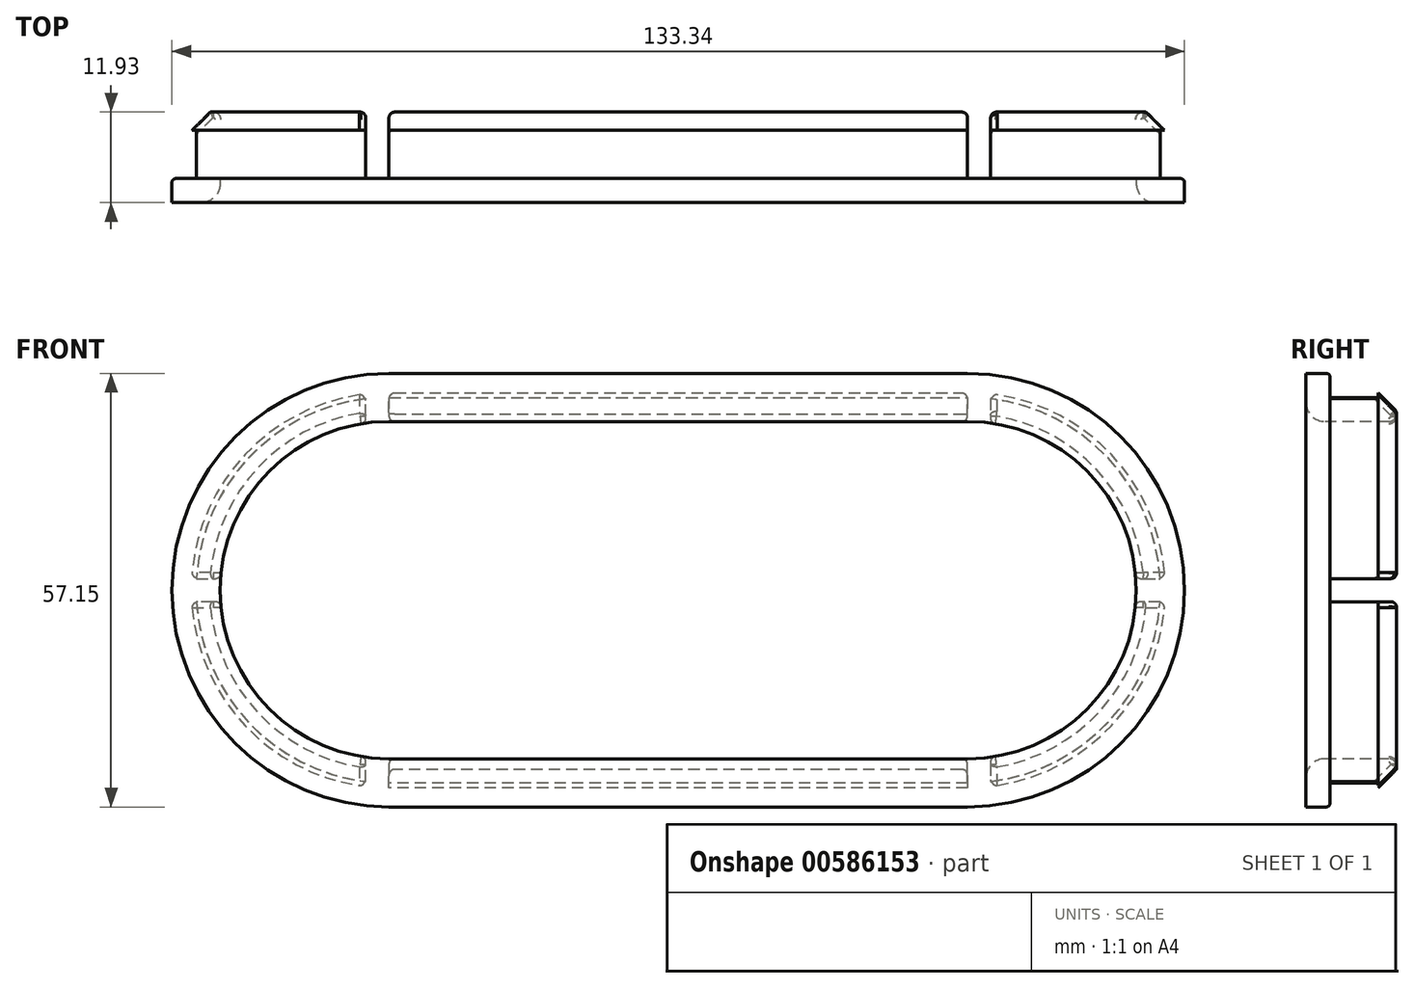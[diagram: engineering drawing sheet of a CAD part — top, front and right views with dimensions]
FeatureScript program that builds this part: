
annotation { "Feature Type Name" : "Feature", "Feature Type Description" : "" }
export const myFeature = defineFeature(function(context is Context, id is Id, definition is map)
    precondition{}
    {
        {
            var Q0;
            Q0=qCreatedBy(makeId("Front.planeOp"),FACE);
            var sketch = newSketch(context, id + "F0", { "sketchPlane" : qUnion([Q0])});
            skArc(sketch, "E0", {"start": v(-38.1, 28.58) * mm, "mid": v(-66.68, 0) * mm, "end": v(-38.1, -28.58) * mm});
            skArc(sketch, "E1", {"start": v(38.1, -28.58) * mm, "mid": v(66.68, 0) * mm, "end": v(38.1, 28.58) * mm});
            skLineSegment(sketch, "E2", {"start": v(-38.1, 28.58) * mm, "end": v(38.1, 28.58) * mm});
            skLineSegment(sketch, "E3", {"start": v(38.1, -28.58) * mm, "end": v(-38.1, -28.58) * mm});
            skArc(sketch, "E4", {"start": v(-38.1, 25.27) * mm, "mid": v(-63.37, 0) * mm, "end": v(-38.1, -25.27) * mm});
            skArc(sketch, "E5", {"start": v(38.1, -25.27) * mm, "mid": v(63.37, 0) * mm, "end": v(38.1, 25.27) * mm});
            skLineSegment(sketch, "E6", {"start": v(-38.1, 25.27) * mm, "end": v(38.1, 25.27) * mm});
            skLineSegment(sketch, "E7", {"start": v(38.1, -25.27) * mm, "end": v(-38.1, -25.27) * mm});
            skArc(sketch, "E8", {"start": v(-38.1, 22.23) * mm, "mid": v(-60.33, 0) * mm, "end": v(-38.1, -22.23) * mm});
            skArc(sketch, "E9", {"start": v(38.1, -22.23) * mm, "mid": v(60.33, 0) * mm, "end": v(38.1, 22.23) * mm});
            skLineSegment(sketch, "E10", {"start": v(-38.1, 22.23) * mm, "end": v(38.1, 22.23) * mm});
            skLineSegment(sketch, "E11", {"start": v(-38.1, -22.23) * mm, "end": v(38.1, -22.23) * mm});
            skSolve(sketch);
        }
        {
            var Q0;
            Q0 = qSketchRegion(id + "F0", true);
            extrude(context, id + "F1", {"entities" : qUnion([Q0]), "depth" : 3.17 * mm, "offsetDistance" : 25.4 * mm});
        }
        {
            var Q0;
            Q0=makeQuery(id+"F1.opExtrude","CAP_FACE",FACE,{"disambiguationData":[OSD([sQuery(id+"F0.wireOp",EDGE,"E0"),sQuery(id+"F0.wireOp",EDGE,"E1"),sQuery(id+"F0.wireOp",EDGE,"E2"),sQuery(id+"F0.wireOp",EDGE,"E3"),sQuery(id+"F0.wireOp",EDGE,"E4"),sQuery(id+"F0.wireOp",EDGE,"E5"),sQuery(id+"F0.wireOp",EDGE,"E6"),sQuery(id+"F0.wireOp",EDGE,"E7")])],"isStart":false});
            var sketch = newSketch(context, id + "F2", { "sketchPlane" : qUnion([Q0])});
            skArc(sketch, "E12", {"start": v(-38.1, 22.23) * mm, "mid": v(-60.33, 0) * mm, "end": v(-38.1, -22.23) * mm});
            skArc(sketch, "E13", {"start": v(38.1, -22.23) * mm, "mid": v(60.33, 0) * mm, "end": v(38.1, 22.23) * mm});
            skLineSegment(sketch, "E14", {"start": v(-38.1, 22.22) * mm, "end": v(38.1, 22.23) * mm});
            skLineSegment(sketch, "E15", {"start": v(38.1, -22.23) * mm, "end": v(-38.1, -22.23) * mm});
            skArc(sketch, "E16", {"start": v(-38.1, 25.4) * mm, "mid": v(-63.5, 0) * mm, "end": v(-38.1, -25.4) * mm});
            skArc(sketch, "E17", {"start": v(38.1, -25.4) * mm, "mid": v(63.5, 0) * mm, "end": v(38.1, 25.4) * mm});
            skLineSegment(sketch, "E18", {"start": v(-38.1, 25.4) * mm, "end": v(38.1, 25.4) * mm});
            skLineSegment(sketch, "E19", {"start": v(38.1, -25.4) * mm, "end": v(-38.1, -25.4) * mm});
            skSolve(sketch);
        }
        {
            var Q0;
            Q0 = qSketchRegion(id + "F2", true);
            extrude(context, id + "F3", {"entities" : qUnion([Q0]), "operationType" : NewBodyOperationType.ADD, "oppositeDirection" : true, "depth" : 11.94 * mm, "offsetDistance" : 25.4 * mm});
        }
        {
            var Q0;
            Q0=makeQuery(id+"F3.opExtrude","CAP_FACE",FACE,{"disambiguationData":[OSD([sQuery(id+"F2.wireOp",EDGE,"E12"),sQuery(id+"F2.wireOp",EDGE,"E13"),sQuery(id+"F2.wireOp",EDGE,"E14"),sQuery(id+"F2.wireOp",EDGE,"E15"),sQuery(id+"F2.wireOp",EDGE,"E16"),sQuery(id+"F2.wireOp",EDGE,"E17"),sQuery(id+"F2.wireOp",EDGE,"E18"),sQuery(id+"F2.wireOp",EDGE,"E19")])],"isStart":false});
            var sketch = newSketch(context, id + "F4", { "sketchPlane" : qUnion([Q0])});
            skArc(sketch, "E20", {"start": v(-38.1, 26.16) * mm, "mid": v(-64.26, 0) * mm, "end": v(-38.1, -26.16) * mm});
            skArc(sketch, "E21", {"start": v(38.1, -26.16) * mm, "mid": v(64.26, 0) * mm, "end": v(38.1, 26.16) * mm});
            skLineSegment(sketch, "E22", {"start": v(-38.1, 26.16) * mm, "end": v(38.1, 26.16) * mm});
            skLineSegment(sketch, "E23", {"start": v(38.1, -26.16) * mm, "end": v(-38.1, -26.16) * mm});
            skArc(sketch, "E24", {"start": v(-38.1, 25.4) * mm, "mid": v(-63.5, 0) * mm, "end": v(-38.1, -25.4) * mm});
            skArc(sketch, "E25", {"start": v(38.1, -25.4) * mm, "mid": v(63.5, 0) * mm, "end": v(38.1, 25.4) * mm});
            skLineSegment(sketch, "E26", {"start": v(-38.1, 25.4) * mm, "end": v(38.1, 25.4) * mm});
            skLineSegment(sketch, "E27", {"start": v(136.2, 25.4) * mm, "end": v(136.2, -25.4) * mm});
            skLineSegment(sketch, "E28", {"start": v(38.1, -25.4) * mm, "end": v(-38.1, -25.4) * mm});
            skSolve(sketch);
        }
        {
            var Q0;
            Q0 = qSketchRegion(id + "F4", true);
            extrude(context, id + "F5", {"entities" : qUnion([Q0]), "operationType" : NewBodyOperationType.ADD, "oppositeDirection" : true, "depth" : 2.41 * mm, "offsetDistance" : 25.4 * mm});
        }
        {
            var Q0;
            Q0=makeQuery(id+"F5.opExtrude","CAP_EDGE",EDGE,{"disambiguationData":[OSD([sQuery(id+"F4.wireOp",EDGE,"E22")])],"isStart":true});
            chamfer(context, id + "F6", {"entities" : qUnion([Q0]), "width" : 2.54 * mm, "tangentPropagation" : true});
        }
        {
            var Q0;
            Q0=makeQuery(id+"F3.opExtrude","CAP_EDGE",EDGE,{"disambiguationData":[OSD([sQuery(id+"F2.wireOp",EDGE,"E14")])],"isStart":true});
            fillet(context, id + "F7", {"entities" : qUnion([Q0]), "radius" : 2.54 * mm, "tangentPropagation" : true, "allowEdgeOverflow" : false});
        }
        {
            var Q0;
            Q0=qCreatedBy(makeId("Front.planeOp"),FACE);
            var sketch = newSketch(context, id + "F8", { "sketchPlane" : qUnion([Q0])});
            skLineSegment(sketch, "E29", {"start": v(101.6, -1.52) * mm, "end": v(-101.6, -1.52) * mm});
            skLineSegment(sketch, "E30", {"start": v(-101.6, -1.52) * mm, "end": v(-101.6, 1.52) * mm});
            skLineSegment(sketch, "E31", {"start": v(-101.6, 1.52) * mm, "end": v(101.6, 1.52) * mm});
            skLineSegment(sketch, "E32", {"start": v(101.6, 1.52) * mm, "end": v(101.6, -1.52) * mm});
            skSolve(sketch);
        }
        {
            var Q0;
            Q0 = qSketchRegion(id + "F8", true);
            extrude(context, id + "F9", {"entities" : qUnion([Q0]), "operationType" : NewBodyOperationType.REMOVE, "oppositeDirection" : true, "depth" : 25.4 * mm, "offsetDistance" : 25.4 * mm});
        }
        {
            var Q0;
            Q0=qCreatedBy(makeId("Front.planeOp"),FACE);
            var sketch = newSketch(context, id + "F10", { "sketchPlane" : qUnion([Q0])});
            skLineSegment(sketch, "E33", {"start": v(41.15, 38.1) * mm, "end": v(41.15, -38.1) * mm});
            skLineSegment(sketch, "E34", {"start": v(41.15, -38.1) * mm, "end": v(38.1, -38.1) * mm});
            skLineSegment(sketch, "E35", {"start": v(38.1, -38.1) * mm, "end": v(38.1, 38.1) * mm});
            skLineSegment(sketch, "E36", {"start": v(38.1, 38.1) * mm, "end": v(41.15, 38.1) * mm});
            skLineSegment(sketch, "E37", {"start": v(-38.1, 38.1) * mm, "end": v(-38.1, -38.1) * mm});
            skLineSegment(sketch, "E38", {"start": v(-38.1, -38.1) * mm, "end": v(-41.15, -38.1) * mm});
            skLineSegment(sketch, "E39", {"start": v(-41.15, -38.1) * mm, "end": v(-41.15, 38.1) * mm});
            skLineSegment(sketch, "E40", {"start": v(-41.15, 38.1) * mm, "end": v(-38.1, 38.1) * mm});
            skSolve(sketch);
        }
        {
            var Q0;
            Q0 = qSketchRegion(id + "F10", true);
            extrude(context, id + "F11", {"entities" : qUnion([Q0]), "operationType" : NewBodyOperationType.REMOVE, "oppositeDirection" : true, "depth" : 25.4 * mm, "offsetDistance" : 25.4 * mm});
        }
        {
            var Q0;
            Q0=makeQuery(id+"F3.opExtrude","CAP_EDGE",EDGE,{"disambiguationData":[OSD([sQuery(id+"F2.wireOp",EDGE,"E14")])],"isStart":false});
            var Q1;
            {var subQ0=sQuery(id+"F2.wireOp",EDGE,"E14");var subQ1=sQuery(id+"F2.wireOp",EDGE,"E13");Q1=makeQuery(id+"F9.boolean.opBoolean","SPLIT",EDGE,{"disambiguationData":[TD([makeQuery(id+"F3.opExtrude","SWEPT_FACE",FACE,{"disambiguationData":[OSD([subQ0])]})])],"derivedFrom":makeQuery(id+"F3.opExtrude","CAP_EDGE",EDGE,{"disambiguationData":[OSD([subQ1])],"isStart":false})});}
            var Q2;
            {var subQ0=sQuery(id+"F2.wireOp",EDGE,"E15");var subQ1=sQuery(id+"F2.wireOp",EDGE,"E13");Q2=makeQuery(id+"F9.boolean.opBoolean","SPLIT",EDGE,{"disambiguationData":[TD([makeQuery(id+"F3.opExtrude","SWEPT_FACE",FACE,{"disambiguationData":[OSD([subQ0])]})])],"derivedFrom":makeQuery(id+"F3.opExtrude","CAP_EDGE",EDGE,{"disambiguationData":[OSD([subQ1])],"isStart":false})});}
            var Q3;
            Q3=makeQuery(id+"F3.opExtrude","CAP_EDGE",EDGE,{"disambiguationData":[OSD([sQuery(id+"F2.wireOp",EDGE,"E15")])],"isStart":false});
            var Q4;
            {var subQ0=sQuery(id+"F2.wireOp",EDGE,"E15");var subQ1=sQuery(id+"F2.wireOp",EDGE,"E12");Q4=makeQuery(id+"F9.boolean.opBoolean","SPLIT",EDGE,{"disambiguationData":[TD([makeQuery(id+"F3.opExtrude","SWEPT_FACE",FACE,{"disambiguationData":[OSD([subQ0])]})])],"derivedFrom":makeQuery(id+"F3.opExtrude","CAP_EDGE",EDGE,{"disambiguationData":[OSD([subQ1])],"isStart":false})});}
            var Q5;
            {var subQ0=sQuery(id+"F2.wireOp",EDGE,"E14");var subQ1=sQuery(id+"F2.wireOp",EDGE,"E12");Q5=makeQuery(id+"F9.boolean.opBoolean","SPLIT",EDGE,{"disambiguationData":[TD([makeQuery(id+"F3.opExtrude","SWEPT_FACE",FACE,{"disambiguationData":[OSD([subQ0])]})])],"derivedFrom":makeQuery(id+"F3.opExtrude","CAP_EDGE",EDGE,{"disambiguationData":[OSD([subQ1])],"isStart":false})});}
            fillet(context, id + "F12", {"entities" : qUnion([Q0, Q1, Q2, Q3, Q4, Q5]), "radius" : 1.02 * mm, "tangentPropagation" : true, "allowEdgeOverflow" : false});
        }
        {
            var Q0;
            {var subQ0=sQuery(id+"F4.wireOp",EDGE,"E22");Q0=makeQuery(id+"F6.opChamfer","BLEND_EDGE",EDGE,{"blendedFrom":[makeQuery(id+"F5.opExtrude","CAP_EDGE",EDGE,{"disambiguationData":[OSD([subQ0])],"isStart":true}),makeQuery(id+"F5.boolean.opBoolean","MERGE",FACE,{"derivedFrom":[makeQuery(id+"F3.opExtrude","CAP_FACE",FACE,{"disambiguationData":[OSD([sQuery(id+"F2.wireOp",EDGE,"E12"),sQuery(id+"F2.wireOp",EDGE,"E13"),sQuery(id+"F2.wireOp",EDGE,"E14"),sQuery(id+"F2.wireOp",EDGE,"E15"),sQuery(id+"F2.wireOp",EDGE,"E16"),sQuery(id+"F2.wireOp",EDGE,"E17"),sQuery(id+"F2.wireOp",EDGE,"E18"),sQuery(id+"F2.wireOp",EDGE,"E19")])],"isStart":false}),makeQuery(id+"F5.opExtrude","CAP_FACE",FACE,{"disambiguationData":[OSD([sQuery(id+"F4.wireOp",EDGE,"E20"),sQuery(id+"F4.wireOp",EDGE,"E21"),subQ0,sQuery(id+"F4.wireOp",EDGE,"E23"),sQuery(id+"F4.wireOp",EDGE,"E24"),sQuery(id+"F4.wireOp",EDGE,"E25"),sQuery(id+"F4.wireOp",EDGE,"E26"),sQuery(id+"F4.wireOp",EDGE,"E28")])],"isStart":true})]})],"blendedInto":[makeQuery(id+"F5.boolean.opBoolean","MERGE",FACE,{"derivedFrom":[makeQuery(id+"F3.opExtrude","CAP_FACE",FACE,{"disambiguationData":[OSD([sQuery(id+"F2.wireOp",EDGE,"E12"),sQuery(id+"F2.wireOp",EDGE,"E13"),sQuery(id+"F2.wireOp",EDGE,"E14"),sQuery(id+"F2.wireOp",EDGE,"E15"),sQuery(id+"F2.wireOp",EDGE,"E16"),sQuery(id+"F2.wireOp",EDGE,"E17"),sQuery(id+"F2.wireOp",EDGE,"E18"),sQuery(id+"F2.wireOp",EDGE,"E19")])],"isStart":false}),makeQuery(id+"F5.opExtrude","CAP_FACE",FACE,{"disambiguationData":[OSD([sQuery(id+"F4.wireOp",EDGE,"E20"),sQuery(id+"F4.wireOp",EDGE,"E21"),subQ0,sQuery(id+"F4.wireOp",EDGE,"E23"),sQuery(id+"F4.wireOp",EDGE,"E24"),sQuery(id+"F4.wireOp",EDGE,"E25"),sQuery(id+"F4.wireOp",EDGE,"E26"),sQuery(id+"F4.wireOp",EDGE,"E28")])],"isStart":true})]})]});}
            var Q1;
            {var subQ0=sQuery(id+"F4.wireOp",EDGE,"E22");var subQ1=sQuery(id+"F4.wireOp",EDGE,"E20");var subQ2=makeQuery(id+"F3.opExtrude","CAP_FACE",FACE,{"disambiguationData":[OSD([sQuery(id+"F2.wireOp",EDGE,"E12"),sQuery(id+"F2.wireOp",EDGE,"E13"),sQuery(id+"F2.wireOp",EDGE,"E14"),sQuery(id+"F2.wireOp",EDGE,"E15"),sQuery(id+"F2.wireOp",EDGE,"E16"),sQuery(id+"F2.wireOp",EDGE,"E17"),sQuery(id+"F2.wireOp",EDGE,"E18"),sQuery(id+"F2.wireOp",EDGE,"E19")])],"isStart":false});var subQ3=makeQuery(id+"F5.opExtrude","CAP_FACE",FACE,{"disambiguationData":[OSD([subQ1,sQuery(id+"F4.wireOp",EDGE,"E21"),subQ0,sQuery(id+"F4.wireOp",EDGE,"E23"),sQuery(id+"F4.wireOp",EDGE,"E24"),sQuery(id+"F4.wireOp",EDGE,"E25"),sQuery(id+"F4.wireOp",EDGE,"E26"),sQuery(id+"F4.wireOp",EDGE,"E28")])],"isStart":true});Q1=makeQuery(id+"F9.boolean.opBoolean","SPLIT",EDGE,{"disambiguationData":[TD([makeQuery(id+"F6.opChamfer","BLEND_FACE",FACE,{"disambiguationData":[OSD([subQ0])]})])],"derivedFrom":makeQuery(id+"F6.opChamfer","BLEND_EDGE",EDGE,{"blendedFrom":[makeQuery(id+"F5.opExtrude","CAP_EDGE",EDGE,{"disambiguationData":[OSD([subQ1])],"isStart":true}),makeQuery(id+"F5.boolean.opBoolean","MERGE",FACE,{"derivedFrom":[subQ2,subQ3]})],"blendedInto":[makeQuery(id+"F5.boolean.opBoolean","MERGE",FACE,{"derivedFrom":[subQ2,subQ3]})]})});}
            var Q2;
            {var subQ0=sQuery(id+"F2.wireOp",EDGE,"E13");var subQ1=makeQuery(id+"F3.opExtrude","SWEPT_FACE",FACE,{"disambiguationData":[OSD([subQ0])]});var subQ2=sQuery(id+"F4.wireOp",EDGE,"E20");var subQ4=sQuery(id+"F2.wireOp",EDGE,"E17");var subQ5=sQuery(id+"F4.wireOp",EDGE,"E28");var subQ6=sQuery(id+"F4.wireOp",EDGE,"E26");var subQ7=sQuery(id+"F4.wireOp",EDGE,"E25");var subQ8=sQuery(id+"F4.wireOp",EDGE,"E24");var subQ9=sQuery(id+"F4.wireOp",EDGE,"E23");var subQ10=sQuery(id+"F4.wireOp",EDGE,"E22");var subQ11=sQuery(id+"F4.wireOp",EDGE,"E21");var subQ12=sQuery(id+"F2.wireOp",EDGE,"E15");var subQ13=sQuery(id+"F2.wireOp",EDGE,"E12");var subQ14=makeQuery(id+"F3.opExtrude","CAP_FACE",FACE,{"disambiguationData":[OSD([subQ13,subQ0,sQuery(id+"F2.wireOp",EDGE,"E14"),subQ12,sQuery(id+"F2.wireOp",EDGE,"E16"),subQ4,sQuery(id+"F2.wireOp",EDGE,"E18"),sQuery(id+"F2.wireOp",EDGE,"E19")])],"isStart":false});var subQ15=makeQuery(id+"F5.opExtrude","CAP_FACE",FACE,{"disambiguationData":[OSD([subQ2,subQ11,subQ10,subQ9,subQ8,subQ7,subQ6,subQ5])],"isStart":true});var subQ18=makeQuery(id+"F3.opExtrude","SWEPT_FACE",FACE,{"disambiguationData":[OSD([subQ12])]});Q2=makeQuery(id+"F12.opFillet","BLEND_EDGE",EDGE,{"blendedFrom":[makeQuery(id+"F9.boolean.opBoolean","SPLIT",EDGE,{"disambiguationData":[TD([subQ18])],"derivedFrom":makeQuery(id+"F3.opExtrude","CAP_EDGE",EDGE,{"disambiguationData":[OSD([subQ0])],"isStart":false})}),makeQuery(id+"F11.boolean.opBoolean","SPLIT",FACE,{"disambiguationData":[TD([subQ1])],"derivedFrom":makeQuery(id+"F9.boolean.opBoolean","SPLIT",FACE,{"disambiguationData":[TD([subQ18])],"derivedFrom":makeQuery(id+"F5.boolean.opBoolean","MERGE",FACE,{"derivedFrom":[subQ14,subQ15]})})})],"blendedInto":[makeQuery(id+"F11.boolean.opBoolean","SPLIT",FACE,{"disambiguationData":[TD([subQ1])],"derivedFrom":makeQuery(id+"F9.boolean.opBoolean","SPLIT",FACE,{"disambiguationData":[TD([subQ18])],"derivedFrom":makeQuery(id+"F5.boolean.opBoolean","MERGE",FACE,{"derivedFrom":[subQ14,subQ15]})})})]});}
            var Q3;
            {var subQ0=sQuery(id+"F2.wireOp",EDGE,"E15");var subQ1=makeQuery(id+"F3.opExtrude","SWEPT_FACE",FACE,{"disambiguationData":[OSD([subQ0])]});var subQ2=sQuery(id+"F4.wireOp",EDGE,"E23");var subQ4=sQuery(id+"F4.wireOp",EDGE,"E20");var subQ5=sQuery(id+"F2.wireOp",EDGE,"E13");var subQ6=sQuery(id+"F4.wireOp",EDGE,"E21");var subQ7=sQuery(id+"F2.wireOp",EDGE,"E12");Q3=makeQuery(id+"F12.opFillet","BLEND_EDGE",EDGE,{"blendedFrom":[makeQuery(id+"F3.opExtrude","CAP_EDGE",EDGE,{"disambiguationData":[OSD([subQ0])],"isStart":false}),makeQuery(id+"F11.boolean.opBoolean","SPLIT",FACE,{"disambiguationData":[TD([subQ1])],"derivedFrom":makeQuery(id+"F9.boolean.opBoolean","SPLIT",FACE,{"disambiguationData":[TD([subQ1])],"derivedFrom":makeQuery(id+"F5.boolean.opBoolean","MERGE",FACE,{"derivedFrom":[makeQuery(id+"F3.opExtrude","CAP_FACE",FACE,{"disambiguationData":[OSD([subQ7,subQ5,sQuery(id+"F2.wireOp",EDGE,"E14"),subQ0,sQuery(id+"F2.wireOp",EDGE,"E16"),sQuery(id+"F2.wireOp",EDGE,"E17"),sQuery(id+"F2.wireOp",EDGE,"E18"),sQuery(id+"F2.wireOp",EDGE,"E19")])],"isStart":false}),makeQuery(id+"F5.opExtrude","CAP_FACE",FACE,{"disambiguationData":[OSD([subQ4,subQ6,sQuery(id+"F4.wireOp",EDGE,"E22"),subQ2,sQuery(id+"F4.wireOp",EDGE,"E24"),sQuery(id+"F4.wireOp",EDGE,"E25"),sQuery(id+"F4.wireOp",EDGE,"E26"),sQuery(id+"F4.wireOp",EDGE,"E28")])],"isStart":true})]})})})],"blendedInto":[makeQuery(id+"F11.boolean.opBoolean","SPLIT",FACE,{"disambiguationData":[TD([subQ1])],"derivedFrom":makeQuery(id+"F9.boolean.opBoolean","SPLIT",FACE,{"disambiguationData":[TD([subQ1])],"derivedFrom":makeQuery(id+"F5.boolean.opBoolean","MERGE",FACE,{"derivedFrom":[makeQuery(id+"F3.opExtrude","CAP_FACE",FACE,{"disambiguationData":[OSD([subQ7,subQ5,sQuery(id+"F2.wireOp",EDGE,"E14"),subQ0,sQuery(id+"F2.wireOp",EDGE,"E16"),sQuery(id+"F2.wireOp",EDGE,"E17"),sQuery(id+"F2.wireOp",EDGE,"E18"),sQuery(id+"F2.wireOp",EDGE,"E19")])],"isStart":false}),makeQuery(id+"F5.opExtrude","CAP_FACE",FACE,{"disambiguationData":[OSD([subQ4,subQ6,sQuery(id+"F4.wireOp",EDGE,"E22"),subQ2,sQuery(id+"F4.wireOp",EDGE,"E24"),sQuery(id+"F4.wireOp",EDGE,"E25"),sQuery(id+"F4.wireOp",EDGE,"E26"),sQuery(id+"F4.wireOp",EDGE,"E28")])],"isStart":true})]})})})]});}
            var Q4;
            {var subQ0=sQuery(id+"F2.wireOp",EDGE,"E12");var subQ1=makeQuery(id+"F3.opExtrude","SWEPT_FACE",FACE,{"disambiguationData":[OSD([subQ0])]});var subQ2=sQuery(id+"F4.wireOp",EDGE,"E21");var subQ4=sQuery(id+"F2.wireOp",EDGE,"E16");var subQ5=sQuery(id+"F4.wireOp",EDGE,"E28");var subQ6=sQuery(id+"F4.wireOp",EDGE,"E26");var subQ7=sQuery(id+"F4.wireOp",EDGE,"E25");var subQ8=sQuery(id+"F4.wireOp",EDGE,"E24");var subQ9=sQuery(id+"F4.wireOp",EDGE,"E23");var subQ10=sQuery(id+"F4.wireOp",EDGE,"E22");var subQ11=sQuery(id+"F4.wireOp",EDGE,"E20");var subQ12=makeQuery(id+"F5.opExtrude","CAP_FACE",FACE,{"disambiguationData":[OSD([subQ11,subQ2,subQ10,subQ9,subQ8,subQ7,subQ6,subQ5])],"isStart":true});var subQ13=sQuery(id+"F2.wireOp",EDGE,"E15");var subQ14=sQuery(id+"F2.wireOp",EDGE,"E13");var subQ15=makeQuery(id+"F3.opExtrude","CAP_FACE",FACE,{"disambiguationData":[OSD([subQ0,subQ14,sQuery(id+"F2.wireOp",EDGE,"E14"),subQ13,subQ4,sQuery(id+"F2.wireOp",EDGE,"E17"),sQuery(id+"F2.wireOp",EDGE,"E18"),sQuery(id+"F2.wireOp",EDGE,"E19")])],"isStart":false});var subQ18=makeQuery(id+"F3.opExtrude","SWEPT_FACE",FACE,{"disambiguationData":[OSD([subQ13])]});Q4=makeQuery(id+"F12.opFillet","BLEND_EDGE",EDGE,{"blendedFrom":[makeQuery(id+"F9.boolean.opBoolean","SPLIT",EDGE,{"disambiguationData":[TD([subQ18])],"derivedFrom":makeQuery(id+"F3.opExtrude","CAP_EDGE",EDGE,{"disambiguationData":[OSD([subQ0])],"isStart":false})}),makeQuery(id+"F11.boolean.opBoolean","SPLIT",FACE,{"disambiguationData":[TD([subQ1])],"derivedFrom":makeQuery(id+"F9.boolean.opBoolean","SPLIT",FACE,{"disambiguationData":[TD([subQ18])],"derivedFrom":makeQuery(id+"F5.boolean.opBoolean","MERGE",FACE,{"derivedFrom":[subQ15,subQ12]})})})],"blendedInto":[makeQuery(id+"F11.boolean.opBoolean","SPLIT",FACE,{"disambiguationData":[TD([subQ1])],"derivedFrom":makeQuery(id+"F9.boolean.opBoolean","SPLIT",FACE,{"disambiguationData":[TD([subQ18])],"derivedFrom":makeQuery(id+"F5.boolean.opBoolean","MERGE",FACE,{"derivedFrom":[subQ15,subQ12]})})})]});}
            var Q5;
            {var subQ0=sQuery(id+"F2.wireOp",EDGE,"E12");var subQ1=makeQuery(id+"F3.opExtrude","SWEPT_FACE",FACE,{"disambiguationData":[OSD([subQ0])]});var subQ2=sQuery(id+"F4.wireOp",EDGE,"E21");var subQ4=sQuery(id+"F2.wireOp",EDGE,"E16");var subQ5=sQuery(id+"F4.wireOp",EDGE,"E28");var subQ6=sQuery(id+"F4.wireOp",EDGE,"E26");var subQ7=sQuery(id+"F4.wireOp",EDGE,"E25");var subQ8=sQuery(id+"F4.wireOp",EDGE,"E24");var subQ9=sQuery(id+"F4.wireOp",EDGE,"E23");var subQ10=sQuery(id+"F4.wireOp",EDGE,"E22");var subQ11=sQuery(id+"F4.wireOp",EDGE,"E20");var subQ12=makeQuery(id+"F5.opExtrude","CAP_FACE",FACE,{"disambiguationData":[OSD([subQ11,subQ2,subQ10,subQ9,subQ8,subQ7,subQ6,subQ5])],"isStart":true});var subQ13=sQuery(id+"F2.wireOp",EDGE,"E14");var subQ14=sQuery(id+"F2.wireOp",EDGE,"E13");var subQ15=makeQuery(id+"F3.opExtrude","CAP_FACE",FACE,{"disambiguationData":[OSD([subQ0,subQ14,subQ13,sQuery(id+"F2.wireOp",EDGE,"E15"),subQ4,sQuery(id+"F2.wireOp",EDGE,"E17"),sQuery(id+"F2.wireOp",EDGE,"E18"),sQuery(id+"F2.wireOp",EDGE,"E19")])],"isStart":false});var subQ18=makeQuery(id+"F3.opExtrude","SWEPT_FACE",FACE,{"disambiguationData":[OSD([subQ13])]});Q5=makeQuery(id+"F12.opFillet","BLEND_EDGE",EDGE,{"blendedFrom":[makeQuery(id+"F9.boolean.opBoolean","SPLIT",EDGE,{"disambiguationData":[TD([subQ18])],"derivedFrom":makeQuery(id+"F3.opExtrude","CAP_EDGE",EDGE,{"disambiguationData":[OSD([subQ0])],"isStart":false})}),makeQuery(id+"F11.boolean.opBoolean","SPLIT",FACE,{"disambiguationData":[TD([subQ1])],"derivedFrom":makeQuery(id+"F9.boolean.opBoolean","SPLIT",FACE,{"disambiguationData":[TD([subQ18])],"derivedFrom":makeQuery(id+"F5.boolean.opBoolean","MERGE",FACE,{"derivedFrom":[subQ15,subQ12]})})})],"blendedInto":[makeQuery(id+"F11.boolean.opBoolean","SPLIT",FACE,{"disambiguationData":[TD([subQ1])],"derivedFrom":makeQuery(id+"F9.boolean.opBoolean","SPLIT",FACE,{"disambiguationData":[TD([subQ18])],"derivedFrom":makeQuery(id+"F5.boolean.opBoolean","MERGE",FACE,{"derivedFrom":[subQ15,subQ12]})})})]});}
            fillet(context, id + "F13", {"entities" : qUnion([Q0, Q1, Q2, Q3, Q4, Q5]), "radius" : 1.02 * mm, "tangentPropagation" : true, "allowEdgeOverflow" : false});
        }
        {
            var Q0;
            Q0=makeQuery(id+"F1.opExtrude","CAP_EDGE",EDGE,{"disambiguationData":[OSD([sQuery(id+"F0.wireOp",EDGE,"E2")])],"isStart":true});
            fillet(context, id + "F14", {"entities" : qUnion([Q0]), "radius" : 0.5 * mm, "tangentPropagation" : true, "allowEdgeOverflow" : false});
        }
        {
            var Q0;
            Q0=makeQuery(id+"F11.boolean.opBoolean","INTERSECT",EDGE,{"disambiguationData":[OD(0.0)],"derivedFrom":[makeQuery(id+"F3.opExtrude","SWEPT_FACE",FACE,{"disambiguationData":[OSD([sQuery(id+"F2.wireOp",EDGE,"E12")])]}),makeQuery(id+"F11.opExtrude","SWEPT_FACE",FACE,{"disambiguationData":[OSD([sQuery(id+"F10.wireOp",EDGE,"E39")])]})]});
            var Q1;
            {var subQ10=sQuery(id+"F10.wireOp",EDGE,"E35");var subQ11=sQuery(id+"F2.wireOp",EDGE,"E14");Q1=makeQuery(id+"F12.opFillet","BLEND_EDGE",EDGE,{"blendedFrom":[makeQuery(id+"F3.opExtrude","CAP_EDGE",EDGE,{"disambiguationData":[OSD([subQ11])],"isStart":false}),makeQuery(id+"F11.boolean.opBoolean","COPY",FACE,{"disambiguationData":[TD([makeQuery(id+"F3.opExtrude","SWEPT_FACE",FACE,{"disambiguationData":[OSD([subQ11])]})])],"derivedFrom":makeQuery(id+"F11.opExtrude","SWEPT_FACE",FACE,{"disambiguationData":[OSD([subQ10])]})})],"blendedInto":[makeQuery(id+"F11.boolean.opBoolean","COPY",FACE,{"disambiguationData":[TD([makeQuery(id+"F3.opExtrude","SWEPT_FACE",FACE,{"disambiguationData":[OSD([subQ11])]})])],"derivedFrom":makeQuery(id+"F11.opExtrude","SWEPT_FACE",FACE,{"disambiguationData":[OSD([subQ10])]})})]});}
            var Q2;
            {var subQ0=sQuery(id+"F4.wireOp",EDGE,"E28");var subQ1=sQuery(id+"F4.wireOp",EDGE,"E26");var subQ2=sQuery(id+"F4.wireOp",EDGE,"E25");var subQ3=sQuery(id+"F4.wireOp",EDGE,"E24");var subQ4=sQuery(id+"F4.wireOp",EDGE,"E23");var subQ5=sQuery(id+"F4.wireOp",EDGE,"E22");var subQ6=sQuery(id+"F4.wireOp",EDGE,"E21");var subQ7=sQuery(id+"F4.wireOp",EDGE,"E20");var subQ8=makeQuery(id+"F5.opExtrude","CAP_FACE",FACE,{"disambiguationData":[OSD([subQ7,subQ6,subQ5,subQ4,subQ3,subQ2,subQ1,subQ0])],"isStart":true});var subQ9=sQuery(id+"F2.wireOp",EDGE,"E18");var subQ10=sQuery(id+"F2.wireOp",EDGE,"E13");var subQ11=sQuery(id+"F10.wireOp",EDGE,"E35");var subQ12=sQuery(id+"F2.wireOp",EDGE,"E14");var subQ13=makeQuery(id+"F3.opExtrude","CAP_FACE",FACE,{"disambiguationData":[OSD([sQuery(id+"F2.wireOp",EDGE,"E12"),subQ10,subQ12,sQuery(id+"F2.wireOp",EDGE,"E15"),sQuery(id+"F2.wireOp",EDGE,"E16"),sQuery(id+"F2.wireOp",EDGE,"E17"),subQ9,sQuery(id+"F2.wireOp",EDGE,"E19")])],"isStart":false});Q2=makeQuery(id+"F13.opFillet","BLEND_EDGE",EDGE,{"blendedFrom":[makeQuery(id+"F6.opChamfer","BLEND_EDGE",EDGE,{"blendedFrom":[makeQuery(id+"F5.opExtrude","CAP_EDGE",EDGE,{"disambiguationData":[OSD([subQ5])],"isStart":true}),makeQuery(id+"F5.boolean.opBoolean","MERGE",FACE,{"derivedFrom":[subQ13,subQ8]})],"blendedInto":[makeQuery(id+"F5.boolean.opBoolean","MERGE",FACE,{"derivedFrom":[subQ13,subQ8]})]}),makeQuery(id+"F11.boolean.opBoolean","COPY",FACE,{"disambiguationData":[TD([makeQuery(id+"F3.opExtrude","SWEPT_FACE",FACE,{"disambiguationData":[OSD([subQ12])]})])],"derivedFrom":makeQuery(id+"F11.opExtrude","SWEPT_FACE",FACE,{"disambiguationData":[OSD([subQ11])]})})],"blendedInto":[makeQuery(id+"F11.boolean.opBoolean","COPY",FACE,{"disambiguationData":[TD([makeQuery(id+"F3.opExtrude","SWEPT_FACE",FACE,{"disambiguationData":[OSD([subQ12])]})])],"derivedFrom":makeQuery(id+"F11.opExtrude","SWEPT_FACE",FACE,{"disambiguationData":[OSD([subQ11])]})})]});}
            var Q3;
            {var subQ0=sQuery(id+"F4.wireOp",EDGE,"E22");var subQ1=sQuery(id+"F4.wireOp",EDGE,"E20");var subQ2=makeQuery(id+"F3.opExtrude","CAP_FACE",FACE,{"disambiguationData":[OSD([sQuery(id+"F2.wireOp",EDGE,"E12"),sQuery(id+"F2.wireOp",EDGE,"E13"),sQuery(id+"F2.wireOp",EDGE,"E14"),sQuery(id+"F2.wireOp",EDGE,"E15"),sQuery(id+"F2.wireOp",EDGE,"E16"),sQuery(id+"F2.wireOp",EDGE,"E17"),sQuery(id+"F2.wireOp",EDGE,"E18"),sQuery(id+"F2.wireOp",EDGE,"E19")])],"isStart":false});var subQ3=makeQuery(id+"F5.opExtrude","CAP_FACE",FACE,{"disambiguationData":[OSD([subQ1,sQuery(id+"F4.wireOp",EDGE,"E21"),subQ0,sQuery(id+"F4.wireOp",EDGE,"E23"),sQuery(id+"F4.wireOp",EDGE,"E24"),sQuery(id+"F4.wireOp",EDGE,"E25"),sQuery(id+"F4.wireOp",EDGE,"E26"),sQuery(id+"F4.wireOp",EDGE,"E28")])],"isStart":true});Q3=makeQuery(id+"F13.opFillet","BLEND_EDGE",EDGE,{"blendedFrom":[makeQuery(id+"F9.boolean.opBoolean","SPLIT",EDGE,{"disambiguationData":[TD([makeQuery(id+"F6.opChamfer","BLEND_FACE",FACE,{"disambiguationData":[OSD([subQ0])]})])],"derivedFrom":makeQuery(id+"F6.opChamfer","BLEND_EDGE",EDGE,{"blendedFrom":[makeQuery(id+"F5.opExtrude","CAP_EDGE",EDGE,{"disambiguationData":[OSD([subQ1])],"isStart":true}),makeQuery(id+"F5.boolean.opBoolean","MERGE",FACE,{"derivedFrom":[subQ2,subQ3]})],"blendedInto":[makeQuery(id+"F5.boolean.opBoolean","MERGE",FACE,{"derivedFrom":[subQ2,subQ3]})]})}),makeQuery(id+"F11.boolean.opBoolean","COPY",FACE,{"disambiguationData":[OD(1.0)],"derivedFrom":makeQuery(id+"F11.opExtrude","SWEPT_FACE",FACE,{"disambiguationData":[OSD([sQuery(id+"F10.wireOp",EDGE,"E33")])]})})],"blendedInto":[makeQuery(id+"F11.boolean.opBoolean","COPY",FACE,{"disambiguationData":[OD(1.0)],"derivedFrom":makeQuery(id+"F11.opExtrude","SWEPT_FACE",FACE,{"disambiguationData":[OSD([sQuery(id+"F10.wireOp",EDGE,"E33")])]})})]});}
            var Q4;
            {var subQ0=sQuery(id+"F2.wireOp",EDGE,"E14");var subQ1=sQuery(id+"F2.wireOp",EDGE,"E13");Q4=makeQuery(id+"F12.opFillet","BLEND_EDGE",EDGE,{"blendedFrom":[makeQuery(id+"F9.boolean.opBoolean","SPLIT",EDGE,{"disambiguationData":[TD([makeQuery(id+"F3.opExtrude","SWEPT_FACE",FACE,{"disambiguationData":[OSD([subQ0])]})])],"derivedFrom":makeQuery(id+"F3.opExtrude","CAP_EDGE",EDGE,{"disambiguationData":[OSD([subQ1])],"isStart":false})}),makeQuery(id+"F11.boolean.opBoolean","COPY",FACE,{"disambiguationData":[OD(1.0)],"derivedFrom":makeQuery(id+"F11.opExtrude","SWEPT_FACE",FACE,{"disambiguationData":[OSD([sQuery(id+"F10.wireOp",EDGE,"E33")])]})})],"blendedInto":[makeQuery(id+"F11.boolean.opBoolean","COPY",FACE,{"disambiguationData":[OD(1.0)],"derivedFrom":makeQuery(id+"F11.opExtrude","SWEPT_FACE",FACE,{"disambiguationData":[OSD([sQuery(id+"F10.wireOp",EDGE,"E33")])]})})]});}
            var Q5;
            {var subQ9=sQuery(id+"F2.wireOp",EDGE,"E15");var subQ10=sQuery(id+"F2.wireOp",EDGE,"E13");var subQ12=makeQuery(id+"F3.opExtrude","SWEPT_FACE",FACE,{"disambiguationData":[OSD([subQ10])]});var subQ14=sQuery(id+"F8.wireOp",EDGE,"E29");var subQ15=makeQuery(id+"F9.opExtrude","SWEPT_FACE",FACE,{"disambiguationData":[OSD([subQ14])]});Q5=makeQuery(id+"F12.opFillet","BLEND_EDGE",EDGE,{"blendedFrom":[makeQuery(id+"F9.boolean.opBoolean","SPLIT",EDGE,{"disambiguationData":[TD([makeQuery(id+"F3.opExtrude","SWEPT_FACE",FACE,{"disambiguationData":[OSD([subQ9])]})])],"derivedFrom":makeQuery(id+"F3.opExtrude","CAP_EDGE",EDGE,{"disambiguationData":[OSD([subQ10])],"isStart":false})}),makeQuery(id+"F9.boolean.opBoolean","COPY",FACE,{"disambiguationData":[TD([subQ12])],"derivedFrom":subQ15})],"blendedInto":[makeQuery(id+"F9.boolean.opBoolean","COPY",FACE,{"disambiguationData":[TD([subQ12])],"derivedFrom":subQ15})]});}
            var Q6;
            Q6=makeQuery(id+"F9.boolean.opBoolean","INTERSECT",EDGE,{"derivedFrom":[makeQuery(id+"F6.opChamfer","BLEND_FACE",FACE,{"disambiguationData":[OSD([sQuery(id+"F4.wireOp",EDGE,"E20")])]}),makeQuery(id+"F9.opExtrude","SWEPT_FACE",FACE,{"disambiguationData":[OSD([sQuery(id+"F8.wireOp",EDGE,"E29")])]})]});
            var Q7;
            {var subQ9=sQuery(id+"F2.wireOp",EDGE,"E14");var subQ10=sQuery(id+"F2.wireOp",EDGE,"E13");var subQ12=makeQuery(id+"F3.opExtrude","SWEPT_FACE",FACE,{"disambiguationData":[OSD([subQ10])]});var subQ14=sQuery(id+"F8.wireOp",EDGE,"E31");var subQ15=makeQuery(id+"F9.opExtrude","SWEPT_FACE",FACE,{"disambiguationData":[OSD([subQ14])]});Q7=makeQuery(id+"F12.opFillet","BLEND_EDGE",EDGE,{"blendedFrom":[makeQuery(id+"F9.boolean.opBoolean","SPLIT",EDGE,{"disambiguationData":[TD([makeQuery(id+"F3.opExtrude","SWEPT_FACE",FACE,{"disambiguationData":[OSD([subQ9])]})])],"derivedFrom":makeQuery(id+"F3.opExtrude","CAP_EDGE",EDGE,{"disambiguationData":[OSD([subQ10])],"isStart":false})}),makeQuery(id+"F9.boolean.opBoolean","COPY",FACE,{"disambiguationData":[TD([subQ12])],"derivedFrom":subQ15})],"blendedInto":[makeQuery(id+"F9.boolean.opBoolean","COPY",FACE,{"disambiguationData":[TD([subQ12])],"derivedFrom":subQ15})]});}
            var Q8;
            {var subQ0=sQuery(id+"F2.wireOp",EDGE,"E17");var subQ1=sQuery(id+"F4.wireOp",EDGE,"E28");var subQ2=sQuery(id+"F4.wireOp",EDGE,"E26");var subQ3=sQuery(id+"F4.wireOp",EDGE,"E25");var subQ4=sQuery(id+"F4.wireOp",EDGE,"E24");var subQ5=sQuery(id+"F4.wireOp",EDGE,"E23");var subQ6=sQuery(id+"F4.wireOp",EDGE,"E22");var subQ7=sQuery(id+"F4.wireOp",EDGE,"E21");var subQ8=sQuery(id+"F4.wireOp",EDGE,"E20");var subQ9=sQuery(id+"F2.wireOp",EDGE,"E13");var subQ10=makeQuery(id+"F3.opExtrude","CAP_FACE",FACE,{"disambiguationData":[OSD([sQuery(id+"F2.wireOp",EDGE,"E12"),subQ9,sQuery(id+"F2.wireOp",EDGE,"E14"),sQuery(id+"F2.wireOp",EDGE,"E15"),sQuery(id+"F2.wireOp",EDGE,"E16"),subQ0,sQuery(id+"F2.wireOp",EDGE,"E18"),sQuery(id+"F2.wireOp",EDGE,"E19")])],"isStart":false});var subQ12=makeQuery(id+"F5.opExtrude","CAP_FACE",FACE,{"disambiguationData":[OSD([subQ8,subQ7,subQ6,subQ5,subQ4,subQ3,subQ2,subQ1])],"isStart":true});var subQ13=sQuery(id+"F8.wireOp",EDGE,"E31");var subQ14=makeQuery(id+"F9.opExtrude","SWEPT_FACE",FACE,{"disambiguationData":[OSD([subQ13])]});Q8=makeQuery(id+"F13.opFillet","BLEND_EDGE",EDGE,{"blendedFrom":[makeQuery(id+"F9.boolean.opBoolean","SPLIT",EDGE,{"disambiguationData":[TD([makeQuery(id+"F6.opChamfer","BLEND_FACE",FACE,{"disambiguationData":[OSD([subQ6])]})])],"derivedFrom":makeQuery(id+"F6.opChamfer","BLEND_EDGE",EDGE,{"blendedFrom":[makeQuery(id+"F5.opExtrude","CAP_EDGE",EDGE,{"disambiguationData":[OSD([subQ8])],"isStart":true}),makeQuery(id+"F5.boolean.opBoolean","MERGE",FACE,{"derivedFrom":[subQ10,subQ12]})],"blendedInto":[makeQuery(id+"F5.boolean.opBoolean","MERGE",FACE,{"derivedFrom":[subQ10,subQ12]})]})}),makeQuery(id+"F9.boolean.opBoolean","COPY",FACE,{"disambiguationData":[TD([makeQuery(id+"F3.opExtrude","SWEPT_FACE",FACE,{"disambiguationData":[OSD([subQ9])]})])],"derivedFrom":subQ14})],"blendedInto":[makeQuery(id+"F9.boolean.opBoolean","COPY",FACE,{"disambiguationData":[TD([makeQuery(id+"F3.opExtrude","SWEPT_FACE",FACE,{"disambiguationData":[OSD([subQ9])]})])],"derivedFrom":subQ14})]});}
            var Q9;
            {var subQ0=sQuery(id+"F2.wireOp",EDGE,"E15");var subQ1=sQuery(id+"F2.wireOp",EDGE,"E13");Q9=makeQuery(id+"F12.opFillet","BLEND_EDGE",EDGE,{"blendedFrom":[makeQuery(id+"F9.boolean.opBoolean","SPLIT",EDGE,{"disambiguationData":[TD([makeQuery(id+"F3.opExtrude","SWEPT_FACE",FACE,{"disambiguationData":[OSD([subQ0])]})])],"derivedFrom":makeQuery(id+"F3.opExtrude","CAP_EDGE",EDGE,{"disambiguationData":[OSD([subQ1])],"isStart":false})}),makeQuery(id+"F11.boolean.opBoolean","COPY",FACE,{"disambiguationData":[OD(0.0)],"derivedFrom":makeQuery(id+"F11.opExtrude","SWEPT_FACE",FACE,{"disambiguationData":[OSD([sQuery(id+"F10.wireOp",EDGE,"E33")])]})})],"blendedInto":[makeQuery(id+"F11.boolean.opBoolean","COPY",FACE,{"disambiguationData":[OD(0.0)],"derivedFrom":makeQuery(id+"F11.opExtrude","SWEPT_FACE",FACE,{"disambiguationData":[OSD([sQuery(id+"F10.wireOp",EDGE,"E33")])]})})]});}
            var Q10;
            {var subQ0=sQuery(id+"F4.wireOp",EDGE,"E23");var subQ7=sQuery(id+"F4.wireOp",EDGE,"E20");Q10=makeQuery(id+"F11.boolean.opBoolean","INTERSECT",EDGE,{"derivedFrom":[makeQuery(id+"F9.boolean.opBoolean","SPLIT",FACE,{"disambiguationData":[TD([makeQuery(id+"F6.opChamfer","BLEND_FACE",FACE,{"disambiguationData":[OSD([subQ0])]})])],"derivedFrom":makeQuery(id+"F6.opChamfer","BLEND_FACE",FACE,{"disambiguationData":[OSD([subQ7])]})}),makeQuery(id+"F11.opExtrude","SWEPT_FACE",FACE,{"disambiguationData":[OSD([sQuery(id+"F10.wireOp",EDGE,"E33")])]})]});}
            var Q11;
            {var subQ10=sQuery(id+"F10.wireOp",EDGE,"E35");var subQ11=sQuery(id+"F2.wireOp",EDGE,"E15");Q11=makeQuery(id+"F12.opFillet","BLEND_EDGE",EDGE,{"blendedFrom":[makeQuery(id+"F3.opExtrude","CAP_EDGE",EDGE,{"disambiguationData":[OSD([subQ11])],"isStart":false}),makeQuery(id+"F11.boolean.opBoolean","COPY",FACE,{"disambiguationData":[TD([makeQuery(id+"F3.opExtrude","SWEPT_FACE",FACE,{"disambiguationData":[OSD([subQ11])]})])],"derivedFrom":makeQuery(id+"F11.opExtrude","SWEPT_FACE",FACE,{"disambiguationData":[OSD([subQ10])]})})],"blendedInto":[makeQuery(id+"F11.boolean.opBoolean","COPY",FACE,{"disambiguationData":[TD([makeQuery(id+"F3.opExtrude","SWEPT_FACE",FACE,{"disambiguationData":[OSD([subQ11])]})])],"derivedFrom":makeQuery(id+"F11.opExtrude","SWEPT_FACE",FACE,{"disambiguationData":[OSD([subQ10])]})})]});}
            var Q12;
            Q12=makeQuery(id+"F6.opChamfer","BLEND_EDGE",EDGE,{"blendedFrom":[makeQuery(id+"F5.opExtrude","CAP_EDGE",EDGE,{"disambiguationData":[OSD([sQuery(id+"F4.wireOp",EDGE,"E20")])],"isStart":true}),makeQuery(id+"F5.opExtrude","CAP_EDGE",EDGE,{"disambiguationData":[OSD([sQuery(id+"F4.wireOp",EDGE,"E23")])],"isStart":true})],"blendedInto":[]});
            var Q13;
            {var subQ10=sQuery(id+"F2.wireOp",EDGE,"E15");var subQ11=sQuery(id+"F10.wireOp",EDGE,"E37");Q13=makeQuery(id+"F12.opFillet","BLEND_EDGE",EDGE,{"blendedFrom":[makeQuery(id+"F3.opExtrude","CAP_EDGE",EDGE,{"disambiguationData":[OSD([subQ10])],"isStart":false}),makeQuery(id+"F11.boolean.opBoolean","COPY",FACE,{"disambiguationData":[TD([makeQuery(id+"F3.opExtrude","SWEPT_FACE",FACE,{"disambiguationData":[OSD([subQ10])]})])],"derivedFrom":makeQuery(id+"F11.opExtrude","SWEPT_FACE",FACE,{"disambiguationData":[OSD([subQ11])]})})],"blendedInto":[makeQuery(id+"F11.boolean.opBoolean","COPY",FACE,{"disambiguationData":[TD([makeQuery(id+"F3.opExtrude","SWEPT_FACE",FACE,{"disambiguationData":[OSD([subQ10])]})])],"derivedFrom":makeQuery(id+"F11.opExtrude","SWEPT_FACE",FACE,{"disambiguationData":[OSD([subQ11])]})})]});}
            var Q14;
            Q14=makeQuery(id+"F6.opChamfer","BLEND_EDGE",EDGE,{"blendedFrom":[makeQuery(id+"F5.opExtrude","CAP_EDGE",EDGE,{"disambiguationData":[OSD([sQuery(id+"F4.wireOp",EDGE,"E21")])],"isStart":true}),makeQuery(id+"F5.opExtrude","CAP_EDGE",EDGE,{"disambiguationData":[OSD([sQuery(id+"F4.wireOp",EDGE,"E23")])],"isStart":true})],"blendedInto":[]});
            var Q15;
            {var subQ0=sQuery(id+"F2.wireOp",EDGE,"E15");var subQ1=sQuery(id+"F2.wireOp",EDGE,"E12");Q15=makeQuery(id+"F12.opFillet","BLEND_EDGE",EDGE,{"blendedFrom":[makeQuery(id+"F9.boolean.opBoolean","SPLIT",EDGE,{"disambiguationData":[TD([makeQuery(id+"F3.opExtrude","SWEPT_FACE",FACE,{"disambiguationData":[OSD([subQ0])]})])],"derivedFrom":makeQuery(id+"F3.opExtrude","CAP_EDGE",EDGE,{"disambiguationData":[OSD([subQ1])],"isStart":false})}),makeQuery(id+"F11.boolean.opBoolean","COPY",FACE,{"disambiguationData":[OD(1.0)],"derivedFrom":makeQuery(id+"F11.opExtrude","SWEPT_FACE",FACE,{"disambiguationData":[OSD([sQuery(id+"F10.wireOp",EDGE,"E39")])]})})],"blendedInto":[makeQuery(id+"F11.boolean.opBoolean","COPY",FACE,{"disambiguationData":[OD(1.0)],"derivedFrom":makeQuery(id+"F11.opExtrude","SWEPT_FACE",FACE,{"disambiguationData":[OSD([sQuery(id+"F10.wireOp",EDGE,"E39")])]})})]});}
            var Q16;
            {var subQ0=sQuery(id+"F4.wireOp",EDGE,"E23");var subQ6=sQuery(id+"F4.wireOp",EDGE,"E21");Q16=makeQuery(id+"F11.boolean.opBoolean","INTERSECT",EDGE,{"derivedFrom":[makeQuery(id+"F9.boolean.opBoolean","SPLIT",FACE,{"disambiguationData":[TD([makeQuery(id+"F6.opChamfer","BLEND_FACE",FACE,{"disambiguationData":[OSD([subQ0])]})])],"derivedFrom":makeQuery(id+"F6.opChamfer","BLEND_FACE",FACE,{"disambiguationData":[OSD([subQ6])]})}),makeQuery(id+"F11.opExtrude","SWEPT_FACE",FACE,{"disambiguationData":[OSD([sQuery(id+"F10.wireOp",EDGE,"E39")])]})]});}
            var Q17;
            Q17=makeQuery(id+"F9.boolean.opBoolean","INTERSECT",EDGE,{"disambiguationData":[OD(0.0)],"derivedFrom":[makeQuery(id+"F5.boolean.opBoolean","MERGE",FACE,{"derivedFrom":[makeQuery(id+"F3.opExtrude","CAP_FACE",FACE,{"disambiguationData":[OSD([sQuery(id+"F2.wireOp",EDGE,"E12"),sQuery(id+"F2.wireOp",EDGE,"E13"),sQuery(id+"F2.wireOp",EDGE,"E14"),sQuery(id+"F2.wireOp",EDGE,"E15"),sQuery(id+"F2.wireOp",EDGE,"E16"),sQuery(id+"F2.wireOp",EDGE,"E17"),sQuery(id+"F2.wireOp",EDGE,"E18"),sQuery(id+"F2.wireOp",EDGE,"E19")])],"isStart":false}),makeQuery(id+"F5.opExtrude","CAP_FACE",FACE,{"disambiguationData":[OSD([sQuery(id+"F4.wireOp",EDGE,"E20"),sQuery(id+"F4.wireOp",EDGE,"E21"),sQuery(id+"F4.wireOp",EDGE,"E22"),sQuery(id+"F4.wireOp",EDGE,"E23"),sQuery(id+"F4.wireOp",EDGE,"E24"),sQuery(id+"F4.wireOp",EDGE,"E25"),sQuery(id+"F4.wireOp",EDGE,"E26"),sQuery(id+"F4.wireOp",EDGE,"E28")])],"isStart":true})]}),makeQuery(id+"F9.opExtrude","SWEPT_FACE",FACE,{"disambiguationData":[OSD([sQuery(id+"F8.wireOp",EDGE,"E29")])]})]});
            var Q18;
            Q18=makeQuery(id+"F9.boolean.opBoolean","INTERSECT",EDGE,{"derivedFrom":[makeQuery(id+"F6.opChamfer","BLEND_FACE",FACE,{"disambiguationData":[OSD([sQuery(id+"F4.wireOp",EDGE,"E21")])]}),makeQuery(id+"F9.opExtrude","SWEPT_FACE",FACE,{"disambiguationData":[OSD([sQuery(id+"F8.wireOp",EDGE,"E29")])]})]});
            var Q19;
            Q19=makeQuery(id+"F9.boolean.opBoolean","INTERSECT",EDGE,{"derivedFrom":[makeQuery(id+"F3.opExtrude","SWEPT_FACE",FACE,{"disambiguationData":[OSD([sQuery(id+"F2.wireOp",EDGE,"E12")])]}),makeQuery(id+"F9.opExtrude","SWEPT_FACE",FACE,{"disambiguationData":[OSD([sQuery(id+"F8.wireOp",EDGE,"E31")])]})]});
            var Q20;
            {var subQ10=sQuery(id+"F2.wireOp",EDGE,"E14");var subQ11=sQuery(id+"F2.wireOp",EDGE,"E12");var subQ13=makeQuery(id+"F3.opExtrude","SWEPT_FACE",FACE,{"disambiguationData":[OSD([subQ11])]});var subQ14=sQuery(id+"F8.wireOp",EDGE,"E31");var subQ15=makeQuery(id+"F9.opExtrude","SWEPT_FACE",FACE,{"disambiguationData":[OSD([subQ14])]});Q20=makeQuery(id+"F12.opFillet","BLEND_EDGE",EDGE,{"blendedFrom":[makeQuery(id+"F9.boolean.opBoolean","SPLIT",EDGE,{"disambiguationData":[TD([makeQuery(id+"F3.opExtrude","SWEPT_FACE",FACE,{"disambiguationData":[OSD([subQ10])]})])],"derivedFrom":makeQuery(id+"F3.opExtrude","CAP_EDGE",EDGE,{"disambiguationData":[OSD([subQ11])],"isStart":false})}),makeQuery(id+"F9.boolean.opBoolean","COPY",FACE,{"disambiguationData":[TD([subQ13])],"derivedFrom":subQ15})],"blendedInto":[makeQuery(id+"F9.boolean.opBoolean","COPY",FACE,{"disambiguationData":[TD([subQ13])],"derivedFrom":subQ15})]});}
            var Q21;
            Q21=makeQuery(id+"F9.boolean.opBoolean","INTERSECT",EDGE,{"derivedFrom":[makeQuery(id+"F6.opChamfer","BLEND_FACE",FACE,{"disambiguationData":[OSD([sQuery(id+"F4.wireOp",EDGE,"E21")])]}),makeQuery(id+"F9.opExtrude","SWEPT_FACE",FACE,{"disambiguationData":[OSD([sQuery(id+"F8.wireOp",EDGE,"E31")])]})]});
            var Q22;
            {var subQ0=sQuery(id+"F4.wireOp",EDGE,"E22");var subQ6=sQuery(id+"F4.wireOp",EDGE,"E21");Q22=makeQuery(id+"F11.boolean.opBoolean","INTERSECT",EDGE,{"derivedFrom":[makeQuery(id+"F9.boolean.opBoolean","SPLIT",FACE,{"disambiguationData":[TD([makeQuery(id+"F6.opChamfer","BLEND_FACE",FACE,{"disambiguationData":[OSD([subQ0])]})])],"derivedFrom":makeQuery(id+"F6.opChamfer","BLEND_FACE",FACE,{"disambiguationData":[OSD([subQ6])]})}),makeQuery(id+"F11.opExtrude","SWEPT_FACE",FACE,{"disambiguationData":[OSD([sQuery(id+"F10.wireOp",EDGE,"E39")])]})]});}
            var Q23;
            {var subQ10=sQuery(id+"F2.wireOp",EDGE,"E14");var subQ11=sQuery(id+"F10.wireOp",EDGE,"E37");Q23=makeQuery(id+"F12.opFillet","BLEND_EDGE",EDGE,{"blendedFrom":[makeQuery(id+"F3.opExtrude","CAP_EDGE",EDGE,{"disambiguationData":[OSD([subQ10])],"isStart":false}),makeQuery(id+"F11.boolean.opBoolean","COPY",FACE,{"disambiguationData":[TD([makeQuery(id+"F3.opExtrude","SWEPT_FACE",FACE,{"disambiguationData":[OSD([subQ10])]})])],"derivedFrom":makeQuery(id+"F11.opExtrude","SWEPT_FACE",FACE,{"disambiguationData":[OSD([subQ11])]})})],"blendedInto":[makeQuery(id+"F11.boolean.opBoolean","COPY",FACE,{"disambiguationData":[TD([makeQuery(id+"F3.opExtrude","SWEPT_FACE",FACE,{"disambiguationData":[OSD([subQ10])]})])],"derivedFrom":makeQuery(id+"F11.opExtrude","SWEPT_FACE",FACE,{"disambiguationData":[OSD([subQ11])]})})]});}
            var Q24;
            {var subQ0=sQuery(id+"F4.wireOp",EDGE,"E28");var subQ1=sQuery(id+"F4.wireOp",EDGE,"E26");var subQ2=sQuery(id+"F4.wireOp",EDGE,"E25");var subQ3=sQuery(id+"F4.wireOp",EDGE,"E24");var subQ4=sQuery(id+"F4.wireOp",EDGE,"E23");var subQ5=sQuery(id+"F4.wireOp",EDGE,"E22");var subQ6=sQuery(id+"F4.wireOp",EDGE,"E21");var subQ7=sQuery(id+"F4.wireOp",EDGE,"E20");var subQ8=makeQuery(id+"F5.opExtrude","CAP_FACE",FACE,{"disambiguationData":[OSD([subQ7,subQ6,subQ5,subQ4,subQ3,subQ2,subQ1,subQ0])],"isStart":true});var subQ9=sQuery(id+"F2.wireOp",EDGE,"E18");var subQ10=sQuery(id+"F2.wireOp",EDGE,"E12");var subQ11=sQuery(id+"F2.wireOp",EDGE,"E14");var subQ12=makeQuery(id+"F3.opExtrude","CAP_FACE",FACE,{"disambiguationData":[OSD([subQ10,sQuery(id+"F2.wireOp",EDGE,"E13"),subQ11,sQuery(id+"F2.wireOp",EDGE,"E15"),sQuery(id+"F2.wireOp",EDGE,"E16"),sQuery(id+"F2.wireOp",EDGE,"E17"),subQ9,sQuery(id+"F2.wireOp",EDGE,"E19")])],"isStart":false});var subQ13=sQuery(id+"F10.wireOp",EDGE,"E37");Q24=makeQuery(id+"F13.opFillet","BLEND_EDGE",EDGE,{"blendedFrom":[makeQuery(id+"F6.opChamfer","BLEND_EDGE",EDGE,{"blendedFrom":[makeQuery(id+"F5.opExtrude","CAP_EDGE",EDGE,{"disambiguationData":[OSD([subQ5])],"isStart":true}),makeQuery(id+"F5.boolean.opBoolean","MERGE",FACE,{"derivedFrom":[subQ12,subQ8]})],"blendedInto":[makeQuery(id+"F5.boolean.opBoolean","MERGE",FACE,{"derivedFrom":[subQ12,subQ8]})]}),makeQuery(id+"F11.boolean.opBoolean","COPY",FACE,{"disambiguationData":[TD([makeQuery(id+"F3.opExtrude","SWEPT_FACE",FACE,{"disambiguationData":[OSD([subQ11])]})])],"derivedFrom":makeQuery(id+"F11.opExtrude","SWEPT_FACE",FACE,{"disambiguationData":[OSD([subQ13])]})})],"blendedInto":[makeQuery(id+"F11.boolean.opBoolean","COPY",FACE,{"disambiguationData":[TD([makeQuery(id+"F3.opExtrude","SWEPT_FACE",FACE,{"disambiguationData":[OSD([subQ11])]})])],"derivedFrom":makeQuery(id+"F11.opExtrude","SWEPT_FACE",FACE,{"disambiguationData":[OSD([subQ13])]})})]});}
            fillet(context, id + "F15", {"entities" : qUnion([Q0, Q1, Q2, Q3, Q4, Q5, Q6, Q7, Q8, Q9, Q10, Q11, Q12, Q13, Q14, Q15, Q16, Q17, Q18, Q19, Q20, Q21, Q22, Q23, Q24]), "radius" : 0.76 * mm, "tangentPropagation" : true, "allowEdgeOverflow" : false});
        }
    });
